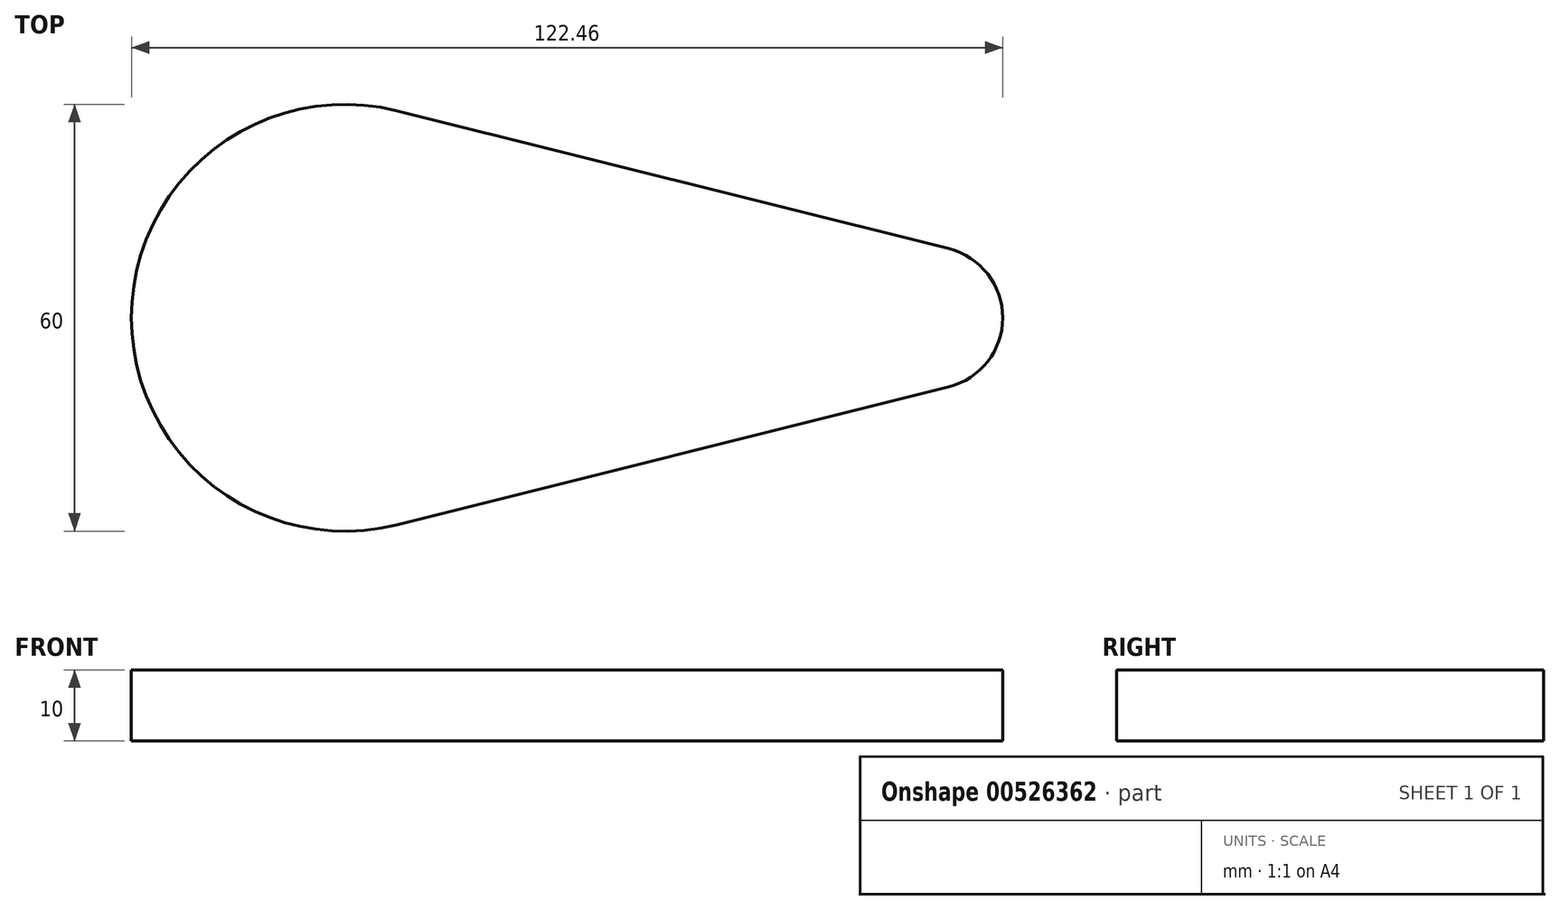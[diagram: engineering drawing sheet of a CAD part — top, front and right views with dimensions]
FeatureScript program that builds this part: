
annotation { "Feature Type Name" : "Feature", "Feature Type Description" : "" }
export const myFeature = defineFeature(function(context is Context, id is Id, definition is map)
    precondition{}
    {
        {
            var Q0;
            Q0=qCreatedBy(makeId("Top.planeOp"),FACE);
            var sketch = newSketch(context, id + "F0", { "sketchPlane" : qUnion([Q0])});
            skCircle(sketch, "E0", {"center": v(-54.54, 0) * mm, "radius": 30 * mm});
            skCircle(sketch, "E1", {"center": v(27.92, 0) * mm, "radius": 10 * mm});
            skLineSegment(sketch, "E2", {"start": v(-47.27, 29.1) * mm, "end": v(30.34, 9.7) * mm});
            skLineSegment(sketch, "E3", {"start": v(-47.27, -29.1) * mm, "end": v(30.34, -9.7) * mm});
            skCircle(sketch, "E4", {"center": v(56.33, 38.08) * mm, "radius": 14.6 * mm});
            skSolve(sketch);
        }
        {
            var Q0;
            {var subQ0=sQuery(id+"F0.wireOp",EDGE,"E1");var subQ1=makeQuery(id+"F0.imprint","INTERSECT",VERTEX,{"derivedFrom":[subQ0,sQuery(id+"F0.wireOp",EDGE,"E2")]});Q0=makeQuery(id+"F0.imprint","IMPRINT",FACE,{"disambiguationData":[TD([[makeQuery(id+"F0.imprint","IMPRINT",EDGE,{"disambiguationData":[TD([[subQ1,-1.0]])],"derivedFrom":subQ0}),1.0]])]});}
            var Q1;
            {var subQ0=sQuery(id+"F0.wireOp",EDGE,"E2");Q1=makeQuery(id+"F0.imprint","IMPRINT",FACE,{"disambiguationData":[TD([[makeQuery(id+"F0.imprint","IMPRINT",EDGE,{"derivedFrom":subQ0}),-1.0]])]});}
            var Q2;
            {var subQ0=sQuery(id+"F0.wireOp",EDGE,"E0");var subQ1=makeQuery(id+"F0.imprint","INTERSECT",VERTEX,{"derivedFrom":[subQ0,sQuery(id+"F0.wireOp",EDGE,"E2")]});Q2=makeQuery(id+"F0.imprint","IMPRINT",FACE,{"disambiguationData":[TD([[makeQuery(id+"F0.imprint","IMPRINT",EDGE,{"disambiguationData":[TD([[subQ1,-1.0]])],"derivedFrom":subQ0}),1.0]])]});}
            extrude(context, id + "F1", {"entities" : qUnion([Q0, Q1, Q2]), "depth" : 10 * mm, "offsetDistance" : 25 * mm});
        }
    });
